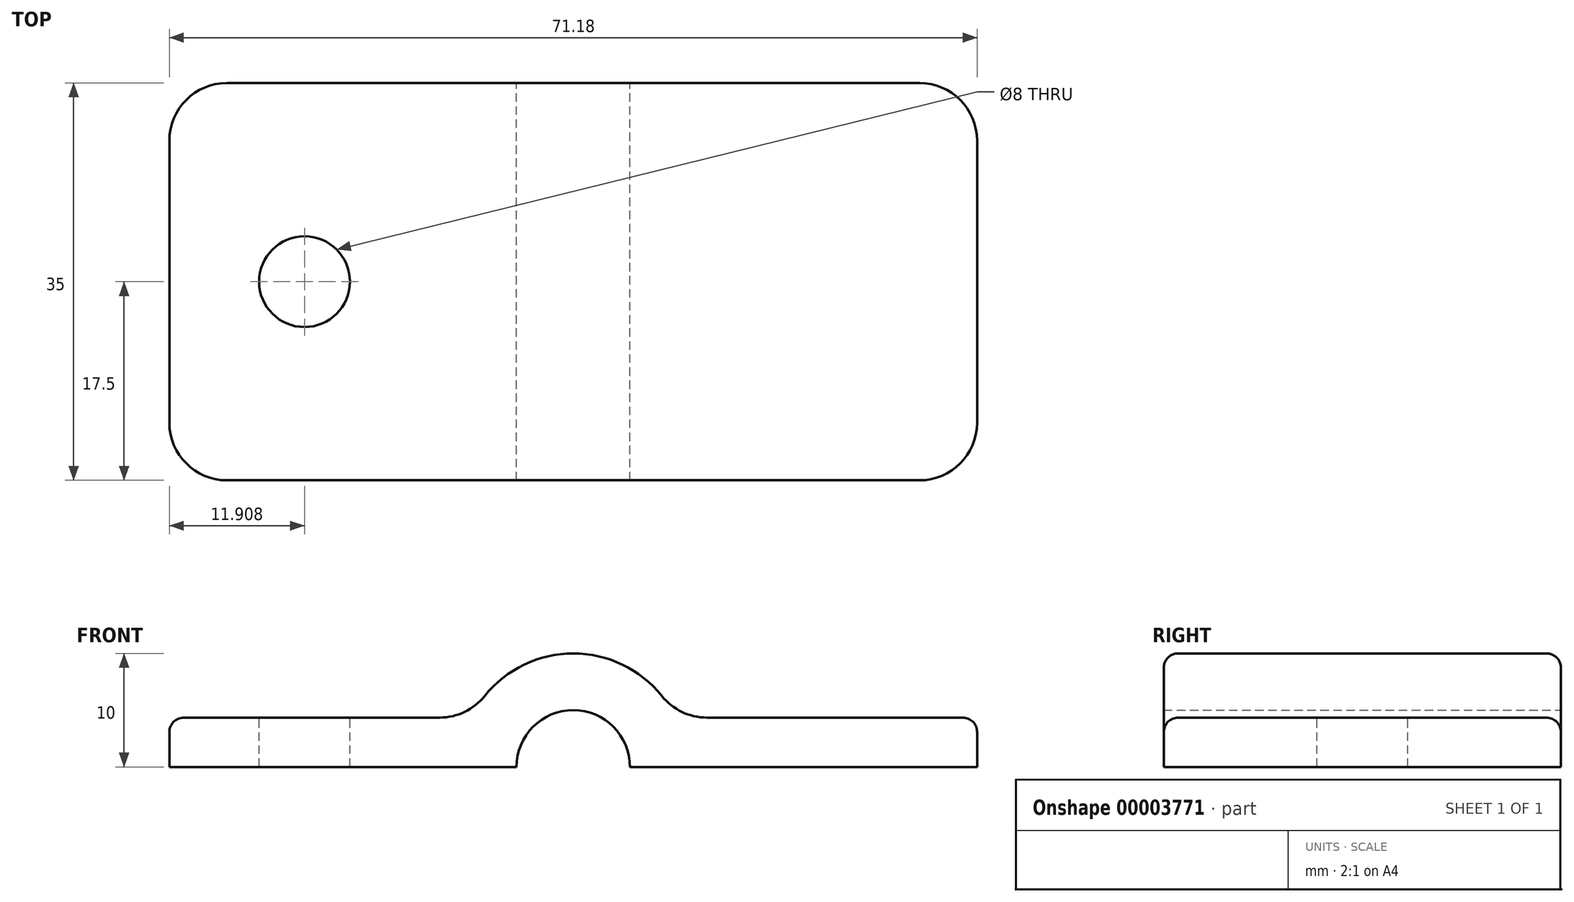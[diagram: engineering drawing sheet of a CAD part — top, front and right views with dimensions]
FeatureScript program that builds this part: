
annotation { "Feature Type Name" : "Feature", "Feature Type Description" : "" }
export const myFeature = defineFeature(function(context is Context, id is Id, definition is map)
    precondition{}
    {
        {
            var Q0;
            Q0=qCreatedBy(makeId("Front.planeOp"),FACE);
            var sketch = newSketch(context, id + "F0", { "sketchPlane" : qUnion([Q0])});
            skArc(sketch, "E0", {"start": v(5, 0) * mm, "mid": v(0, 5) * mm, "end": v(-5, 0) * mm});
            skArc(sketch, "E1.0", {"start": v(9, 4.35) * mm, "mid": v(0, 10) * mm, "end": v(-9, 4.35) * mm});
            skLineSegment(sketch, "E2", {"start": v(-10, 0) * mm, "end": v(-5, 0) * mm});
            skLineSegment(sketch, "E3.trimOffspring", {"start": v(5, 0) * mm, "end": v(10, 0) * mm});
            skLineSegment(sketch, "E4", {"start": v(-10, 0) * mm, "end": v(-35.6, 0) * mm});
            skLineSegment(sketch, "E5", {"start": v(-35.6, 0) * mm, "end": v(-35.6, 4.35) * mm});
            skLineSegment(sketch, "E6", {"start": v(-35.6, 4.35) * mm, "end": v(-9, 4.35) * mm});
            skLineSegment(sketch, "E7", {"start": v(0, 29.6) * mm, "end": v(0, 0) * mm, "construction": true});
            skLineSegment(sketch, "E8.0.MirrorCS", {"start": v(35.6, 4.35) * mm, "end": v(9, 4.35) * mm});
            skLineSegment(sketch, "E9.0.MirrorCS", {"start": v(35.6, 0) * mm, "end": v(35.6, 4.35) * mm});
            skLineSegment(sketch, "E10.0.MirrorCS", {"start": v(10, 0) * mm, "end": v(35.6, 0) * mm});
            skSolve(sketch);
        }
        {
            var Q0;
            Q0=makeQuery(id+"F0.imprint","IMPRINT",FACE,{"disambiguationData":[TD([[makeQuery(id+"F0.imprint","IMPRINT",EDGE,{"derivedFrom":sQuery(id+"F0.wireOp",EDGE,"E0")}),-1.0]])]});
            extrude(context, id + "F1", {"entities" : qUnion([Q0]), "depth" : 35 * mm});
        }
        {
            var Q0;
            Q0=makeQuery(id+"F1.opExtrude","SWEPT_EDGE",EDGE,{"disambiguationData":[OSD([sQuery(id+"F0.wireOp",EDGE,"E1.0"),sQuery(id+"F0.wireOp",EDGE,"E6")])]});
            var Q1;
            Q1=makeQuery(id+"F1.opExtrude","SWEPT_EDGE",EDGE,{"disambiguationData":[OSD([sQuery(id+"F0.wireOp",EDGE,"E1.0"),sQuery(id+"F0.wireOp",EDGE,"E8.0.MirrorCS")])]});
            fillet(context, id + "F2", {"entities" : qUnion([Q0, Q1]), "radius" : 5.08 * mm, "tangentPropagation" : true, "allowEdgeOverflow" : false});
        }
        {
            var Q0;
            Q0=makeQuery(id+"F1.opExtrude","SWEPT_FACE",FACE,{"disambiguationData":[OSD([sQuery(id+"F0.wireOp",EDGE,"E6")])]});
            var sketch = newSketch(context, id + "F3", { "sketchPlane" : qUnion([Q0])});
            skLineSegment(sketch, "E11", {"start": v(-23.68, 0) * mm, "end": v(-23.68, -35) * mm, "construction": true});
            skLineSegment(sketch, "E12", {"start": v(0, 0) * mm, "end": v(0, -35) * mm, "construction": true});
            skLineSegment(sketch, "E13.0.MirrorCS", {"start": v(23.68, 0) * mm, "end": v(23.68, -35) * mm, "construction": true});
            skCircle(sketch, "E14", {"center": v(-23.68, -17.5) * mm, "radius": 4 * mm});
            skCircle(sketch, "E15.0.MirrorC", {"center": v(23.68, -17.5) * mm, "radius": 4 * mm});
            skSolve(sketch);
        }
        {
            var Q0;
            Q0=makeQuery(id+"F3.imprint","IMPRINT",FACE,{"disambiguationData":[TD([[makeQuery(id+"F3.imprint","IMPRINT",EDGE,{"derivedFrom":sQuery(id+"F3.wireOp",EDGE,"E14")}),1.0]])]});
            var Q1;
            Q1=makeQuery(id+"F3.imprint","IMPRINT",FACE,{"disambiguationData":[TD([[makeQuery(id+"F3.imprint","IMPRINT",EDGE,{"derivedFrom":sQuery(id+"F3.wireOp",EDGE,"E15.0.MirrorC")}),-1.0]])]});
            extrude(context, id + "F4", {"entities" : qUnion([Q0, Q1]), "operationType" : NewBodyOperationType.REMOVE, "endBound" : BoundingType.THROUGH_ALL, "oppositeDirection" : true, "depth" : 25.4 * mm});
        }
        {
            var Q0;
            Q0=makeQuery(id+"F1.opExtrude","CAP_EDGE",EDGE,{"disambiguationData":[OSD([sQuery(id+"F0.wireOp",EDGE,"E5")])],"isStart":true});
            var Q1;
            Q1=makeQuery(id+"F1.opExtrude","CAP_EDGE",EDGE,{"disambiguationData":[OSD([sQuery(id+"F0.wireOp",EDGE,"E9.0.MirrorCS")])],"isStart":true});
            var Q2;
            Q2=makeQuery(id+"F1.opExtrude","CAP_EDGE",EDGE,{"disambiguationData":[OSD([sQuery(id+"F0.wireOp",EDGE,"E5")])],"isStart":false});
            var Q3;
            Q3=makeQuery(id+"F1.opExtrude","CAP_EDGE",EDGE,{"disambiguationData":[OSD([sQuery(id+"F0.wireOp",EDGE,"E9.0.MirrorCS")])],"isStart":false});
            fillet(context, id + "F5", {"entities" : qUnion([Q0, Q1, Q2, Q3]), "radius" : 5.08 * mm, "tangentPropagation" : true, "allowEdgeOverflow" : false});
        }
        {
            var Q0;
            Q0=makeQuery(id+"F1.opExtrude","CAP_EDGE",EDGE,{"disambiguationData":[OSD([sQuery(id+"F0.wireOp",EDGE,"E1.0")])],"isStart":true});
            fillet(context, id + "F6", {"entities" : qUnion([Q0]), "radius" : 1.27 * mm, "tangentPropagation" : true, "allowEdgeOverflow" : false});
        }
    });
